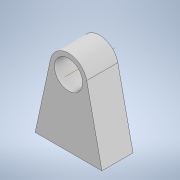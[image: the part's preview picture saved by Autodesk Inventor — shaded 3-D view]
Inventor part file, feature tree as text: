
AUTODESK INVENTOR PART (.ipt)
format: ipt  version: 2021 (Build 250183000, 183)  size: 103,936 bytes
history: native  units: in
note: dims shown in document units (in); Inventor stores cm internally (conversion verified against a paired STEP export)
features: other x2, extrude x1, sketch x1
ambient origin geometry x8: Origin, YZ Plane, XZ Plane, XY Plane, X Axis, Y Axis, Z Axis, Center Point
bodies: Body1 (feature_tree)
feature tree (4):
  other  "Sólido1"
  extrude  "Extrusión1"  Depth=0.2756in
  other  "Eje de trabajo1"
  sketch  "Boceto1"  dims[d0=0.25in d1=0.0394in d2=0.5906in d3=0.2953in d4=0.2953in d5=0.2756in d6=0.0in]
